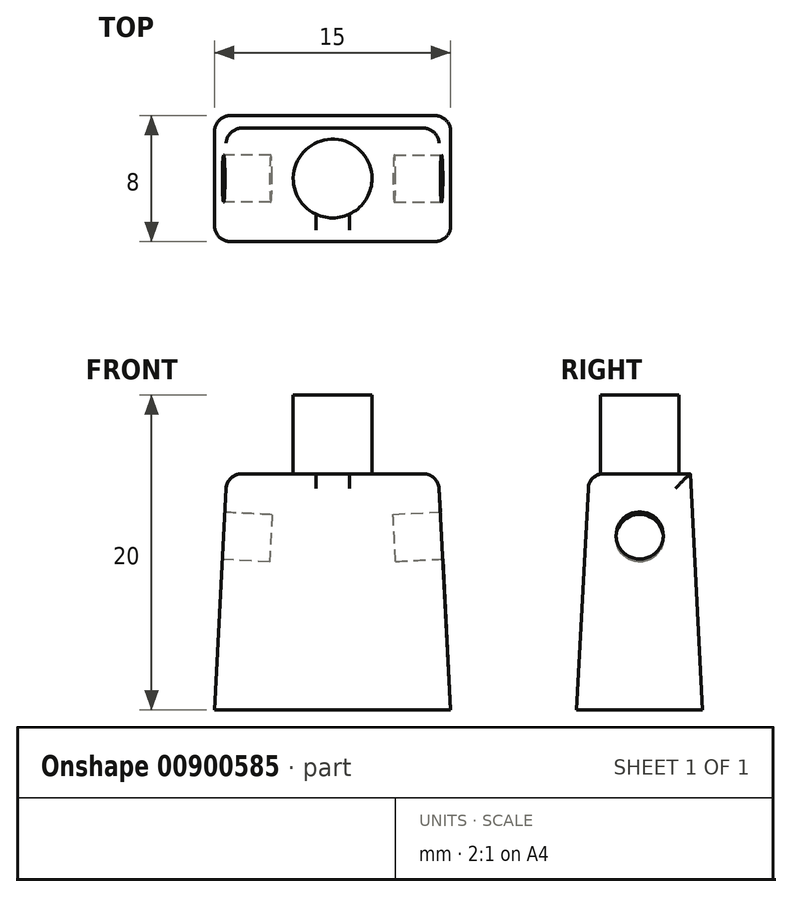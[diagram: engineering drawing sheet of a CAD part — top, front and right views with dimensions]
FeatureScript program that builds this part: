
annotation { "Feature Type Name" : "Feature", "Feature Type Description" : "" }
export const myFeature = defineFeature(function(context is Context, id is Id, definition is map)
    precondition{}
    {
        {
            var Q0;
            Q0=qCreatedBy(makeId("Top.planeOp"),FACE);
            var sketch = newSketch(context, id + "F0", { "sketchPlane" : qUnion([Q0])});
            skLineSegment(sketch, "E0.bottom", {"start": v(7.5, 4) * mm, "end": v(-7.5, 4) * mm});
            skLineSegment(sketch, "E0.top", {"start": v(7.5, -4) * mm, "end": v(-7.5, -4) * mm});
            skLineSegment(sketch, "E0.left", {"start": v(7.5, 4) * mm, "end": v(7.5, -4) * mm});
            skLineSegment(sketch, "E0.right", {"start": v(-7.5, 4) * mm, "end": v(-7.5, -4) * mm});
            skPoint(sketch, "E0.middle", {"position": v(0, 0) * mm});
            skSolve(sketch);
        }
        {
            var Q0;
            Q0 = qSketchRegion(id + "F0", true);
            extrude(context, id + "F1", {"entities" : qUnion([Q0]), "depth" : 15 * mm, "offsetDistance" : 25 * mm, "hasDraft" : true, "draftAngle" : 3 * degree, "draftPullDirection" : true});
        }
        {
            var Q0;
            Q0=makeQuery(id+"F1.opExtrude","CAP_FACE",FACE,{"disambiguationData":[OSD([sQuery(id+"F0.wireOp",EDGE,"E0.bottom"),sQuery(id+"F0.wireOp",EDGE,"E0.top"),sQuery(id+"F0.wireOp",EDGE,"E0.left"),sQuery(id+"F0.wireOp",EDGE,"E0.right")])],"isStart":false});
            var sketch = newSketch(context, id + "F2", { "sketchPlane" : qUnion([Q0])});
            skCircle(sketch, "E1", {"center": v(0, 0) * mm, "radius": 2.5 * mm});
            skSolve(sketch);
        }
        {
            var Q0;
            Q0 = qSketchRegion(id + "F2", true);
            extrude(context, id + "F3", {"entities" : qUnion([Q0]), "operationType" : NewBodyOperationType.ADD, "depth" : 5 * mm, "offsetDistance" : 25 * mm});
        }
        {
            var Q0;
            Q0=makeQuery(id+"F1.opExtrude","SWEPT_EDGE",EDGE,{"disambiguationData":[OSD([sQuery(id+"F0.wireOp",EDGE,"E0.top"),sQuery(id+"F0.wireOp",EDGE,"E0.right")])]});
            var Q1;
            Q1=makeQuery(id+"F1.opExtrude","CAP_EDGE",EDGE,{"disambiguationData":[OSD([sQuery(id+"F0.wireOp",EDGE,"E0.top")])],"isStart":false});
            var Q2;
            Q2=makeQuery(id+"F1.opExtrude","SWEPT_EDGE",EDGE,{"disambiguationData":[OSD([sQuery(id+"F0.wireOp",EDGE,"E0.top"),sQuery(id+"F0.wireOp",EDGE,"E0.left")])]});
            var Q3;
            Q3=makeQuery(id+"F1.opExtrude","CAP_EDGE",EDGE,{"disambiguationData":[OSD([sQuery(id+"F0.wireOp",EDGE,"E0.left")])],"isStart":false});
            var Q4;
            Q4=makeQuery(id+"F1.opExtrude","SWEPT_EDGE",EDGE,{"disambiguationData":[OSD([sQuery(id+"F0.wireOp",EDGE,"E0.bottom"),sQuery(id+"F0.wireOp",EDGE,"E0.left")])]});
            var Q5;
            Q5=makeQuery(id+"F1.opExtrude","CAP_EDGE",EDGE,{"disambiguationData":[OSD([sQuery(id+"F0.wireOp",EDGE,"E0.right")])],"isStart":false});
            var Q6;
            Q6=makeQuery(id+"F1.opExtrude","SWEPT_EDGE",EDGE,{"disambiguationData":[OSD([sQuery(id+"F0.wireOp",EDGE,"E0.bottom"),sQuery(id+"F0.wireOp",EDGE,"E0.right")])]});
            fillet(context, id + "F4", {"entities" : qUnion([Q0, Q1, Q2, Q3, Q4, Q5, Q6]), "radius" : 1 * mm, "tangentPropagation" : true, "allowEdgeOverflow" : false});
        }
        {
            var Q0;
            Q0=makeQuery(id+"F1.opExtrude","SWEPT_FACE",FACE,{"disambiguationData":[OSD([sQuery(id+"F0.wireOp",EDGE,"E0.right")])]});
            var sketch = newSketch(context, id + "F5", { "sketchPlane" : qUnion([Q0])});
            skCircle(sketch, "E2", {"center": v(0, 10.68) * mm, "radius": 1.5 * mm});
            skSolve(sketch);
        }
        {
            var Q0;
            Q0 = qSketchRegion(id + "F5", true);
            extrude(context, id + "F6", {"entities" : qUnion([Q0]), "operationType" : NewBodyOperationType.REMOVE, "oppositeDirection" : true, "depth" : 3 * mm, "offsetDistance" : 25 * mm});
        }
        {
            var Q0;
            Q0=makeQuery(id+"F1.opExtrude","SWEPT_FACE",FACE,{"disambiguationData":[OSD([sQuery(id+"F0.wireOp",EDGE,"E0.left")])]});
            var sketch = newSketch(context, id + "F7", { "sketchPlane" : qUnion([Q0])});
            skCircle(sketch, "E3", {"center": v(0, 10.7) * mm, "radius": 1.5 * mm});
            skSolve(sketch);
        }
        {
            var Q0;
            Q0 = qSketchRegion(id + "F7", true);
            extrude(context, id + "F8", {"entities" : qUnion([Q0]), "operationType" : NewBodyOperationType.REMOVE, "oppositeDirection" : true, "depth" : 3 * mm, "offsetDistance" : 25 * mm});
        }
    });
